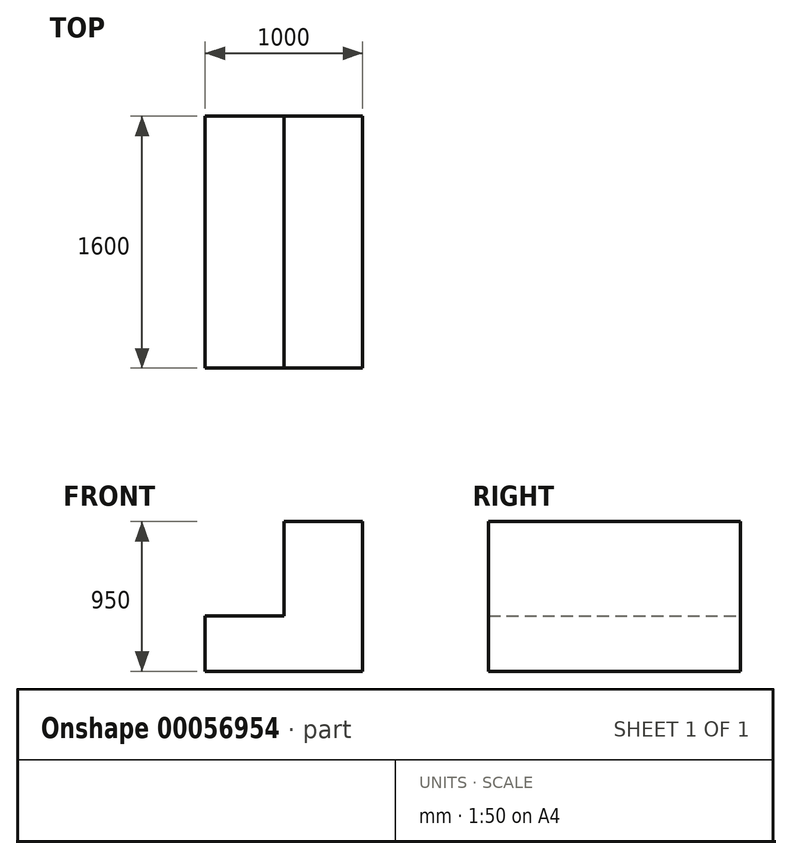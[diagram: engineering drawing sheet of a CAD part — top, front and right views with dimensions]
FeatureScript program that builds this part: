
annotation { "Feature Type Name" : "Feature", "Feature Type Description" : "" }
export const myFeature = defineFeature(function(context is Context, id is Id, definition is map)
    precondition{}
    {
        {
            var Q0;
            Q0=qCreatedBy(makeId("Front.planeOp"),FACE);
            var sketch = newSketch(context, id + "F0", { "sketchPlane" : qUnion([Q0])});
            skLineSegment(sketch, "E0", {"start": v(0, 0) * mm, "end": v(0, 950) * mm});
            skLineSegment(sketch, "E1", {"start": v(0, 950) * mm, "end": v(-500, 950) * mm});
            skLineSegment(sketch, "E2", {"start": v(-500, 950) * mm, "end": v(-500, 350) * mm});
            skLineSegment(sketch, "E3", {"start": v(-500, 350) * mm, "end": v(-1000, 350) * mm});
            skLineSegment(sketch, "E4", {"start": v(-1000, 350) * mm, "end": v(-1000, 0) * mm});
            skLineSegment(sketch, "E5", {"start": v(-1000, 0) * mm, "end": v(0, 0) * mm});
            skSolve(sketch);
        }
        {
            var Q0;
            Q0 = qSketchRegion(id + "F0", true);
            var Q1;
            Q1=makeQuery(id+"F0.imprint","IMPRINT",FACE,{"disambiguationData":[TD([[makeQuery(id+"F0.imprint","IMPRINT",EDGE,{"derivedFrom":sQuery(id+"F0.wireOp",EDGE,"E0")}),1.0]])]});
            extrude(context, id + "F1", {"entities" : qUnion([Q0, Q1]), "depth" : 1600 * mm});
        }
    });
